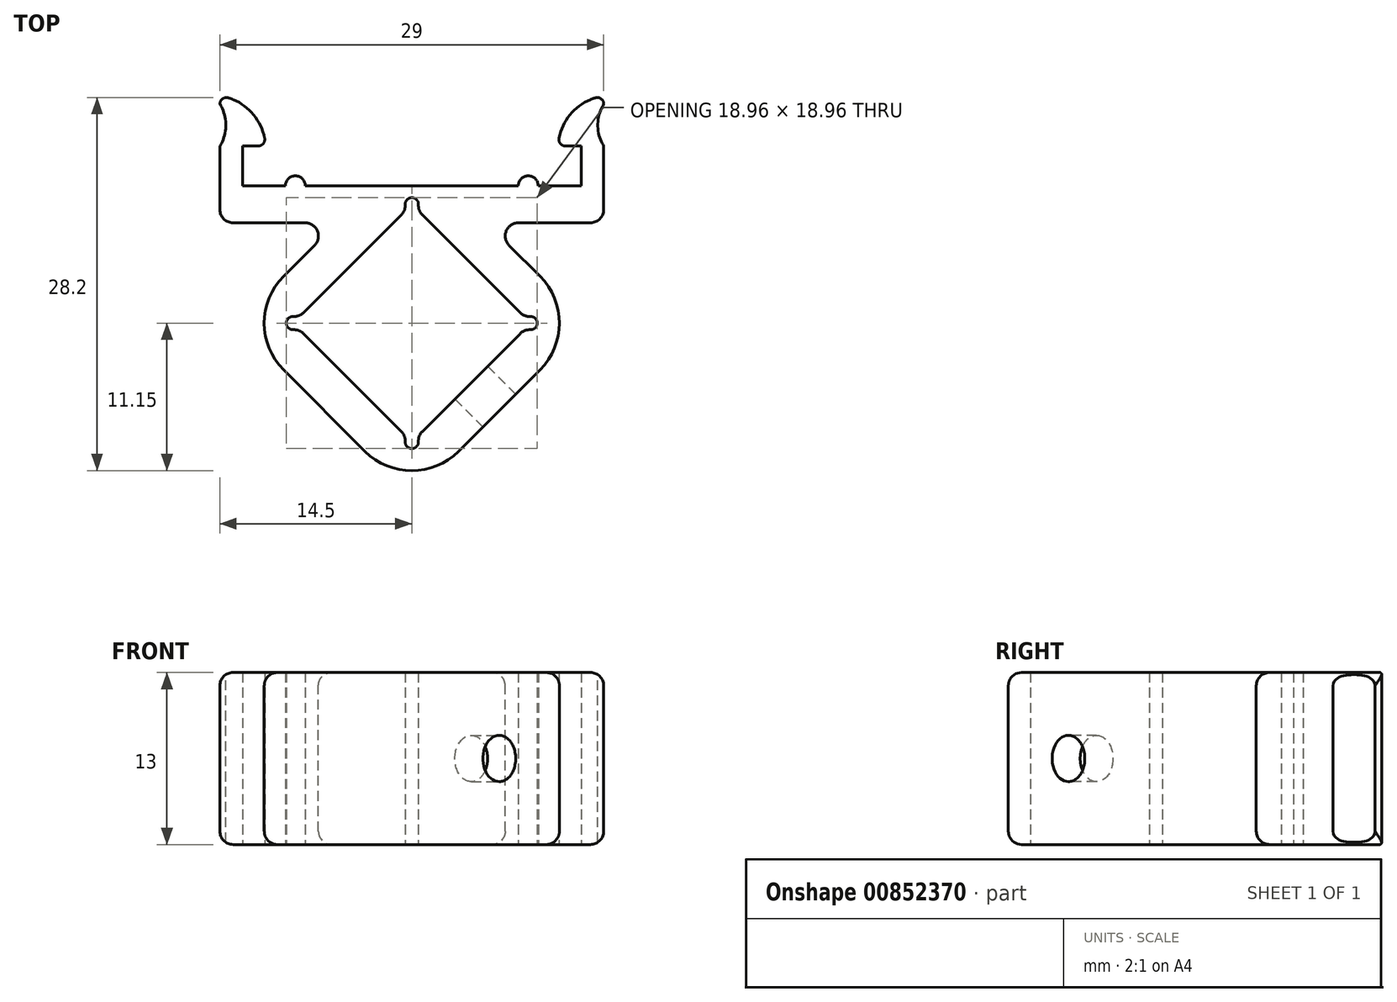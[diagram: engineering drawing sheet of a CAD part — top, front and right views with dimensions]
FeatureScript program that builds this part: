
annotation { "Feature Type Name" : "Feature", "Feature Type Description" : "" }
export const myFeature = defineFeature(function(context is Context, id is Id, definition is map)
    precondition{}
    {
        {
            var Q0;
            Q0=qCreatedBy(makeId("Top.planeOp"),FACE);
            var sketch = newSketch(context, id + "F0", { "sketchPlane" : qUnion([Q0])});
            skLineSegment(sketch, "E0.bottom", {"start": v(-13.5, 0) * mm, "end": v(-5.64, 0) * mm});
            skLineSegment(sketch, "E0.left", {"start": v(-14.5, 1) * mm, "end": v(-14.5, 9.59) * mm});
            skLineSegment(sketch, "E0.right", {"start": v(14.5, 1) * mm, "end": v(14.5, 9.59) * mm});
            skPoint(sketch, "E1.visualSharp", {"position": v(-14.5, 0) * mm});
            skArc(sketch, "E1.filletArc", {"start": v(-14.5, 1) * mm, "mid": v(-14.2, 0.3) * mm, "end": v(-13.5, 0) * mm});
            skPoint(sketch, "E2.visualSharp", {"position": v(14.5, 0) * mm});
            skArc(sketch, "E2.filletArc", {"start": v(13.5, 0) * mm, "mid": v(14.2, 0.3) * mm, "end": v(14.5, 1) * mm});
            skLineSegment(sketch, "E3", {"start": v(-12.8, 2.8) * mm, "end": v(-9.55, 2.8) * mm});
            skPoint(sketch, "E4", {"position": v(0, 2.8) * mm});
            skPoint(sketch, "E4.positionSnap0", {"position": v(0, 2.8) * mm});
            skLineSegment(sketch, "E5", {"start": v(-12.8, 2.8) * mm, "end": v(-12.8, 5.8) * mm});
            skLineSegment(sketch, "E6", {"start": v(-12.8, 5.8) * mm, "end": v(-11.05, 5.8) * mm});
            skLineSegment(sketch, "E7", {"start": v(12.8, 2.8) * mm, "end": v(12.8, 5.8) * mm});
            skLineSegment(sketch, "E8", {"start": v(12.8, 5.8) * mm, "end": v(11.05, 5.8) * mm});
            skArc(sketch, "E9", {"start": v(-11.05, 5.8) * mm, "mid": v(-12.09, 8.32) * mm, "end": v(-14.5, 9.59) * mm});
            skArc(sketch, "E10", {"start": v(14.5, 9.59) * mm, "mid": v(12.09, 8.32) * mm, "end": v(11.05, 5.8) * mm});
            skPoint(sketch, "E11", {"position": v(-8.8, 2.8) * mm});
            skPoint(sketch, "E12", {"position": v(8.8, 2.8) * mm});
            skArc(sketch, "E13", {"start": v(-8.05, 2.8) * mm, "mid": v(-8.8, 3.55) * mm, "end": v(-9.55, 2.8) * mm});
            skArc(sketch, "E14", {"start": v(9.55, 2.8) * mm, "mid": v(8.8, 3.55) * mm, "end": v(8.05, 2.8) * mm});
            skLineSegment(sketch, "E15.trimOffspring", {"start": v(-8.05, 2.8) * mm, "end": v(8.05, 2.8) * mm});
            skLineSegment(sketch, "E16.trimOffspring", {"start": v(9.55, 2.8) * mm, "end": v(12.8, 2.8) * mm});
            skLineSegment(sketch, "E17", {"start": v(0, 2.8) * mm, "end": v(0, 1.4) * mm, "construction": true});
            skLineSegment(sketch, "E18", {"start": v(-0.35, 1.05) * mm, "end": v(-8.63, -7.23) * mm});
            skLineSegment(sketch, "E19", {"start": v(-8.63, -7.93) * mm, "end": v(-0.35, -16.2) * mm});
            skLineSegment(sketch, "E20", {"start": v(0.35, -16.2) * mm, "end": v(8.63, -7.93) * mm});
            skLineSegment(sketch, "E21", {"start": v(8.63, -7.23) * mm, "end": v(0.35, 1.05) * mm});
            skLineSegment(sketch, "E22.0", {"start": v(-5.64, 0) * mm, "end": v(-13.22, -7.58) * mm});
            skLineSegment(sketch, "E22.1", {"start": v(13.22, -7.58) * mm, "end": v(5.64, 0) * mm});
            skLineSegment(sketch, "E22.2", {"start": v(0, -20.8) * mm, "end": v(13.22, -7.58) * mm});
            skLineSegment(sketch, "E22.3", {"start": v(-13.22, -7.58) * mm, "end": v(0, -20.8) * mm});
            skLineSegment(sketch, "E23.trimOffspring", {"start": v(5.64, 0) * mm, "end": v(13.5, 0) * mm});
            skArc(sketch, "E24", {"start": v(0.35, 1.05) * mm, "mid": v(0, 1.9) * mm, "end": v(-0.35, 1.05) * mm});
            skArc(sketch, "E25", {"start": v(8.63, -7.93) * mm, "mid": v(9.48, -7.58) * mm, "end": v(8.63, -7.23) * mm});
            skArc(sketch, "E26", {"start": v(-0.35, -16.2) * mm, "mid": v(0, -17.06) * mm, "end": v(0.35, -16.2) * mm});
            skArc(sketch, "E27", {"start": v(-8.63, -7.23) * mm, "mid": v(-9.48, -7.58) * mm, "end": v(-8.63, -7.93) * mm});
            skLineSegment(sketch, "E28.trimOffspring", {"start": v(0, 0.9) * mm, "end": v(0, 0) * mm, "construction": true});
            skSolve(sketch);
        }
        {
            var Q0;
            Q0=qSketchRegion(id+"F0",true);
            extrude(context, id + "F1", {"entities" : qUnion([Q0]), "depth" : 13 * mm, "offsetDistance" : 25 * mm});
        }
        {
            var Q0;
            Q0=makeQuery(id+"F1.opExtrude","SWEPT_FACE",FACE,{"disambiguationData":[OSD([sQuery(id+"F0.wireOp",EDGE,"E15.trimOffspring")])]});
            var sketch = newSketch(context, id + "F2", { "sketchPlane" : qUnion([Q0])});
            skLineSegment(sketch, "E29", {"start": v(0, 0) * mm, "end": v(0, 13) * mm, "construction": true});
            skCircle(sketch, "E30", {"center": v(0, 6.5) * mm, "radius": 2 * mm});
            skSolve(sketch);
        }
        {
            var Q0;
            Q0=makeQuery(id+"F1.opExtrude","CAP_FACE",FACE,{"disambiguationData":[OSD([sQuery(id+"F0.wireOp",EDGE,"E0.bottom"),sQuery(id+"F0.wireOp",EDGE,"E0.left"),sQuery(id+"F0.wireOp",EDGE,"E0.right"),sQuery(id+"F0.wireOp",EDGE,"E1.filletArc"),sQuery(id+"F0.wireOp",EDGE,"E2.filletArc"),sQuery(id+"F0.wireOp",EDGE,"E3"),sQuery(id+"F0.wireOp",EDGE,"E5"),sQuery(id+"F0.wireOp",EDGE,"E6"),sQuery(id+"F0.wireOp",EDGE,"E7"),sQuery(id+"F0.wireOp",EDGE,"E8"),sQuery(id+"F0.wireOp",EDGE,"E9"),sQuery(id+"F0.wireOp",EDGE,"E10"),sQuery(id+"F0.wireOp",EDGE,"E13"),sQuery(id+"F0.wireOp",EDGE,"E14"),sQuery(id+"F0.wireOp",EDGE,"E15.trimOffspring"),sQuery(id+"F0.wireOp",EDGE,"E16.trimOffspring")])],"isStart":false});
            var sketch = newSketch(context, id + "F3", { "sketchPlane" : qUnion([Q0])});
            skLineSegment(sketch, "E31.0.0", {"start": v(8.05, 2.8) * mm, "end": v(-8.05, 2.8) * mm});
            skArc(sketch, "E31.0.1", {"start": v(-8.05, 2.8) * mm, "mid": v(-8.8, 3.55) * mm, "end": v(-9.55, 2.8) * mm});
            skLineSegment(sketch, "E31.0.2", {"start": v(-9.55, 2.8) * mm, "end": v(-12.8, 2.8) * mm});
            skLineSegment(sketch, "E31.0.3", {"start": v(-12.8, 2.8) * mm, "end": v(-12.8, 5.8) * mm});
            skLineSegment(sketch, "E31.0.4", {"start": v(-12.8, 5.8) * mm, "end": v(-11.05, 5.8) * mm});
            skArc(sketch, "E31.0.5", {"start": v(-11.05, 5.8) * mm, "mid": v(-11.88, 8.06) * mm, "end": v(-13.85, 9.44) * mm});
            skLineSegment(sketch, "E31.0.6", {"start": v(-14.5, 8.97) * mm, "end": v(-14.5, 5.8) * mm});
            skArc(sketch, "E31.0.7", {"start": v(-14.5, 1) * mm, "mid": v(-14.2, 0.3) * mm, "end": v(-13.5, 0) * mm});
            skLineSegment(sketch, "E31.0.8", {"start": v(-13.5, 0) * mm, "end": v(-13.5, 0) * mm});
            skArc(sketch, "E31.0.9", {"start": v(13.5, 0) * mm, "mid": v(14.2, 0.3) * mm, "end": v(14.5, 1) * mm});
            skLineSegment(sketch, "E31.0.10", {"start": v(14.5, 1) * mm, "end": v(14.5, 5.8) * mm});
            skArc(sketch, "E31.0.11", {"start": v(13.85, 9.44) * mm, "mid": v(11.88, 8.06) * mm, "end": v(11.05, 5.8) * mm});
            skLineSegment(sketch, "E31.0.12", {"start": v(11.05, 5.8) * mm, "end": v(12.8, 5.8) * mm});
            skLineSegment(sketch, "E31.0.13", {"start": v(12.8, 5.8) * mm, "end": v(12.8, 2.8) * mm});
            skLineSegment(sketch, "E31.0.14", {"start": v(12.8, 2.8) * mm, "end": v(9.55, 2.8) * mm});
            skArc(sketch, "E31.0.15", {"start": v(9.55, 2.8) * mm, "mid": v(8.8, 3.55) * mm, "end": v(8.05, 2.8) * mm});
            skLineSegment(sketch, "E32", {"start": v(-12.8, 5.8) * mm, "end": v(-15.05, 5.8) * mm, "construction": true});
            skLineSegment(sketch, "E33", {"start": v(-14.5, 5.8) * mm, "end": v(-14.5, 1) * mm});
            skPoint(sketch, "E34.visualSharp", {"position": v(-14.5, 9.59) * mm});
            skArc(sketch, "E34.filletArc", {"start": v(-13.85, 9.44) * mm, "mid": v(-14.3, 9.37) * mm, "end": v(-14.5, 8.97) * mm});
            skPoint(sketch, "E35.visualSharp", {"position": v(14.5, 9.59) * mm});
            skArc(sketch, "E35.filletArc", {"start": v(14.5, 8.97) * mm, "mid": v(14.3, 9.37) * mm, "end": v(13.85, 9.44) * mm});
            skArc(sketch, "E36", {"start": v(-14.5, 5.8) * mm, "mid": v(-14.05, 7.38) * mm, "end": v(-14.5, 8.97) * mm});
            skLineSegment(sketch, "E37", {"start": v(-14.5, 8.97) * mm, "end": v(-14.5, 9.59) * mm});
            skLineSegment(sketch, "E38", {"start": v(-14.5, 9.59) * mm, "end": v(-13.85, 9.44) * mm});
            skLineSegment(sketch, "E39", {"start": v(12.8, 5.8) * mm, "end": v(14.5, 5.8) * mm, "construction": true});
            skLineSegment(sketch, "E40", {"start": v(14.5, 5.8) * mm, "end": v(14.5, 8.97) * mm});
            skArc(sketch, "E41", {"start": v(14.5, 8.97) * mm, "mid": v(14.05, 7.38) * mm, "end": v(14.5, 5.8) * mm});
            skLineSegment(sketch, "E42", {"start": v(13.85, 9.44) * mm, "end": v(14.5, 9.59) * mm});
            skLineSegment(sketch, "E43", {"start": v(14.5, 9.59) * mm, "end": v(14.5, 8.97) * mm});
            skSolve(sketch);
        }
        {
            var Q0;
            Q0=makeQuery(id+"F3.imprint","IMPRINT",FACE,{"disambiguationData":[TD([[makeQuery(id+"F3.imprint","IMPRINT",EDGE,{"derivedFrom":sQuery(id+"F3.wireOp",EDGE,"E31.0.6")}),-1.0]])]});
            var Q1;
            Q1=makeQuery(id+"F3.imprint","IMPRINT",FACE,{"disambiguationData":[TD([[makeQuery(id+"F3.imprint","IMPRINT",EDGE,{"derivedFrom":sQuery(id+"F3.wireOp",EDGE,"E40")}),1.0]])]});
            extrude(context, id + "F4", {"entities" : qUnion([Q0, Q1]), "operationType" : NewBodyOperationType.REMOVE, "endBound" : BoundingType.THROUGH_ALL, "oppositeDirection" : true, "depth" : 25 * mm, "offsetDistance" : 25 * mm});
        }
        {
            var Q0;
            Q0=makeQuery(id+"F1.opExtrude","SWEPT_EDGE",EDGE,{"disambiguationData":[OSD([sQuery(id+"F0.wireOp",EDGE,"E0.left"),sQuery(id+"F0.wireOp",EDGE,"E9")])]});
            var Q1;
            Q1=makeQuery(id+"F1.opExtrude","SWEPT_EDGE",EDGE,{"disambiguationData":[OSD([sQuery(id+"F0.wireOp",EDGE,"E0.right"),sQuery(id+"F0.wireOp",EDGE,"E10")])]});
            fillet(context, id + "F5", {"entities" : qUnion([Q0, Q1]), "radius" : .5 * mm, "tangentPropagation" : true, "allowEdgeOverflow" : false});
        }
        {
            var Q0;
            Q0=makeQuery(id+"F1.opExtrude","SWEPT_EDGE",EDGE,{"disambiguationData":[OSD([sQuery(id+"F0.wireOp",EDGE,"E0.bottom"),sQuery(id+"F0.wireOp",EDGE,"E22.0")])]});
            var Q1;
            Q1=makeQuery(id+"F1.opExtrude","SWEPT_EDGE",EDGE,{"disambiguationData":[OSD([sQuery(id+"F0.wireOp",EDGE,"E22.1"),sQuery(id+"F0.wireOp",EDGE,"E23.trimOffspring")])]});
            fillet(context, id + "F6", {"entities" : qUnion([Q0, Q1]), "radius" : 1 * mm, "tangentPropagation" : true, "allowEdgeOverflow" : false});
        }
        {
            var Q0;
            Q0=makeQuery(id+"F1.opExtrude","SWEPT_EDGE",EDGE,{"disambiguationData":[OSD([sQuery(id+"F0.wireOp",EDGE,"E22.0"),sQuery(id+"F0.wireOp",EDGE,"E22.3")])]});
            var Q1;
            Q1=makeQuery(id+"F1.opExtrude","SWEPT_EDGE",EDGE,{"disambiguationData":[OSD([sQuery(id+"F0.wireOp",EDGE,"E22.2"),sQuery(id+"F0.wireOp",EDGE,"E22.3")])]});
            var Q2;
            Q2=makeQuery(id+"F1.opExtrude","SWEPT_EDGE",EDGE,{"disambiguationData":[OSD([sQuery(id+"F0.wireOp",EDGE,"E22.1"),sQuery(id+"F0.wireOp",EDGE,"E22.2")])]});
            fillet(context, id + "F7", {"entities" : qUnion([Q0, Q1, Q2]), "radius" : 5 * mm, "tangentPropagation" : true, "allowEdgeOverflow" : false});
        }
        {
            var Q0;
            Q0=makeQuery(id+"F1.opExtrude","CAP_EDGE",EDGE,{"disambiguationData":[OSD([sQuery(id+"F0.wireOp",EDGE,"E22.3")])],"isStart":false});
            var Q1;
            Q1=makeQuery(id+"F1.opExtrude","CAP_EDGE",EDGE,{"disambiguationData":[OSD([sQuery(id+"F0.wireOp",EDGE,"E22.3")])],"isStart":true});
            fillet(context, id + "F8", {"entities" : qUnion([Q0, Q1]), "radius" : 1 * mm, "tangentPropagation" : true, "allowEdgeOverflow" : false});
        }
        {
            var Q0;
            Q0=makeQuery(id+"F1.opExtrude","SWEPT_EDGE",EDGE,{"disambiguationData":[OSD([sQuery(id+"F0.wireOp",EDGE,"E6"),sQuery(id+"F0.wireOp",EDGE,"E9")])]});
            var Q1;
            Q1=makeQuery(id+"F1.opExtrude","SWEPT_EDGE",EDGE,{"disambiguationData":[OSD([sQuery(id+"F0.wireOp",EDGE,"E8"),sQuery(id+"F0.wireOp",EDGE,"E10")])]});
            fillet(context, id + "F9", {"entities" : qUnion([Q0, Q1]), "radius" : .5 * mm, "tangentPropagation" : true, "allowEdgeOverflow" : false});
        }
        {
            var Q0;
            Q0=makeQuery(id+"F1.opExtrude","SWEPT_EDGE",EDGE,{"disambiguationData":[OSD([sQuery(id+"F0.wireOp",EDGE,"E18"),sQuery(id+"F0.wireOp",EDGE,"E24")])]});
            var Q1;
            Q1=makeQuery(id+"F1.opExtrude","SWEPT_EDGE",EDGE,{"disambiguationData":[OSD([sQuery(id+"F0.wireOp",EDGE,"E21"),sQuery(id+"F0.wireOp",EDGE,"E24")])]});
            var Q2;
            Q2=makeQuery(id+"F1.opExtrude","SWEPT_EDGE",EDGE,{"disambiguationData":[OSD([sQuery(id+"F0.wireOp",EDGE,"E18"),sQuery(id+"F0.wireOp",EDGE,"E27")])]});
            var Q3;
            Q3=makeQuery(id+"F1.opExtrude","SWEPT_EDGE",EDGE,{"disambiguationData":[OSD([sQuery(id+"F0.wireOp",EDGE,"E19"),sQuery(id+"F0.wireOp",EDGE,"E27")])]});
            var Q4;
            Q4=makeQuery(id+"F1.opExtrude","SWEPT_EDGE",EDGE,{"disambiguationData":[OSD([sQuery(id+"F0.wireOp",EDGE,"E19"),sQuery(id+"F0.wireOp",EDGE,"E26")])]});
            var Q5;
            Q5=makeQuery(id+"F1.opExtrude","SWEPT_EDGE",EDGE,{"disambiguationData":[OSD([sQuery(id+"F0.wireOp",EDGE,"E20"),sQuery(id+"F0.wireOp",EDGE,"E26")])]});
            var Q6;
            Q6=makeQuery(id+"F1.opExtrude","SWEPT_EDGE",EDGE,{"disambiguationData":[OSD([sQuery(id+"F0.wireOp",EDGE,"E21"),sQuery(id+"F0.wireOp",EDGE,"E25")])]});
            var Q7;
            Q7=makeQuery(id+"F1.opExtrude","SWEPT_EDGE",EDGE,{"disambiguationData":[OSD([sQuery(id+"F0.wireOp",EDGE,"E20"),sQuery(id+"F0.wireOp",EDGE,"E25")])]});
            fillet(context, id + "F10", {"entities" : qUnion([Q0, Q1, Q2, Q3, Q4, Q5, Q6, Q7]), "radius" : 1 * mm, "tangentPropagation" : true, "allowEdgeOverflow" : false});
        }
        {
            var Q0;
            Q0=makeQuery(id+"F1.opExtrude","SWEPT_FACE",FACE,{"disambiguationData":[OSD([sQuery(id+"F0.wireOp",EDGE,"E22.2")])]});
            var sketch = newSketch(context, id + "F11", { "sketchPlane" : qUnion([Q0])});
            skLineSegment(sketch, "E44", {"start": v(-1.01, 6.5) * mm, "end": v(-9.71, 6.5) * mm, "construction": true});
            skCircle(sketch, "E45", {"center": v(-5.36, 6.5) * mm, "radius": 1.75 * mm});
            skSolve(sketch);
        }
        {
            var Q0;
            Q0=makeQuery(id+"F11.imprint","IMPRINT",FACE,{"disambiguationData":[TD([[makeQuery(id+"F11.imprint","IMPRINT",EDGE,{"derivedFrom":sQuery(id+"F11.wireOp",EDGE,"E45")}),1.0]])]});
            var Q1;
            Q1=makeQuery(id+"F1.opExtrude","SWEPT_FACE",FACE,{"disambiguationData":[OSD([sQuery(id+"F0.wireOp",EDGE,"E18")])]});
            extrude(context, id + "F12", {"entities" : qUnion([Q0]), "operationType" : NewBodyOperationType.REMOVE, "endBound" : BoundingType.UP_TO_SURFACE, "oppositeDirection" : true, "depth" : 25 * mm, "endBoundEntityFace" : qUnion([Q1]), "offsetDistance" : 25 * mm});
        }
    });
